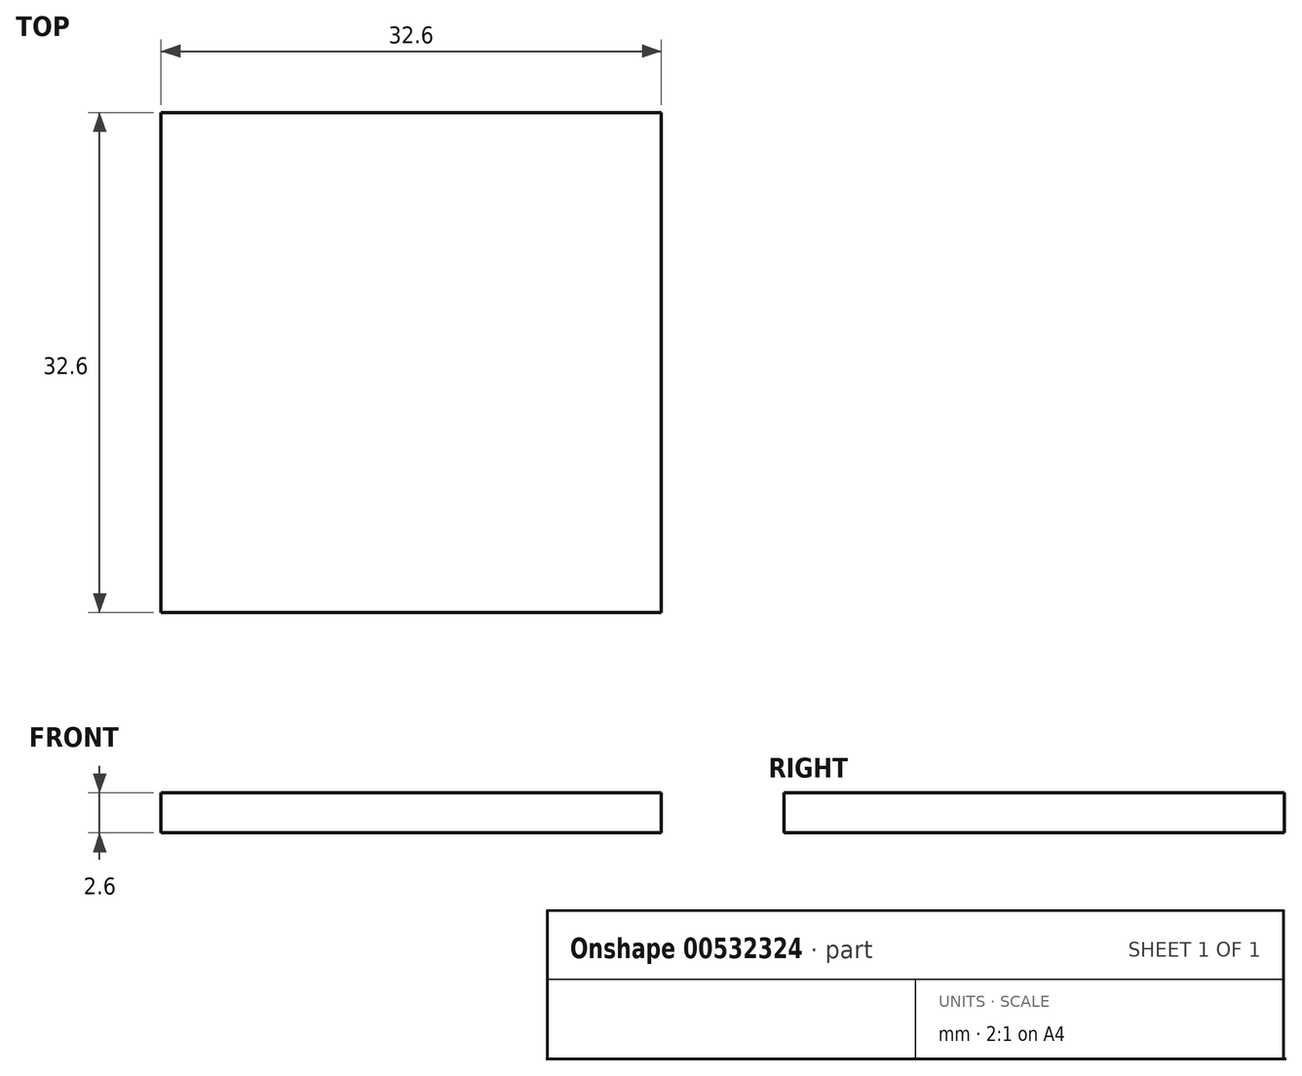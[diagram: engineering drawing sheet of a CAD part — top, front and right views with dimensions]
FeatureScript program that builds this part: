
annotation { "Feature Type Name" : "Feature", "Feature Type Description" : "" }
export const myFeature = defineFeature(function(context is Context, id is Id, definition is map)
    precondition{}
    {
        {
            var Q0;
            Q0=qCreatedBy(makeId("Top.planeOp"),FACE);
            var sketch = newSketch(context, id + "F0", { "sketchPlane" : qUnion([Q0])});
            skLineSegment(sketch, "E0.bottom", {"start": v(0, 0) * mm, "end": v(32.6, 0) * mm});
            skLineSegment(sketch, "E0.top", {"start": v(0, 32.6) * mm, "end": v(32.6, 32.6) * mm});
            skLineSegment(sketch, "E0.left", {"start": v(0, 0) * mm, "end": v(0, 32.6) * mm});
            skLineSegment(sketch, "E0.right", {"start": v(32.6, 0) * mm, "end": v(32.6, 32.6) * mm});
            skSolve(sketch);
        }
        {
            var Q0;
            Q0 = qSketchRegion(id + "F0", true);
            extrude(context, id + "F1", {"entities" : qUnion([Q0]), "depth" : 2.6 * mm, "offsetDistance" : 25.4 * mm});
        }
    });
